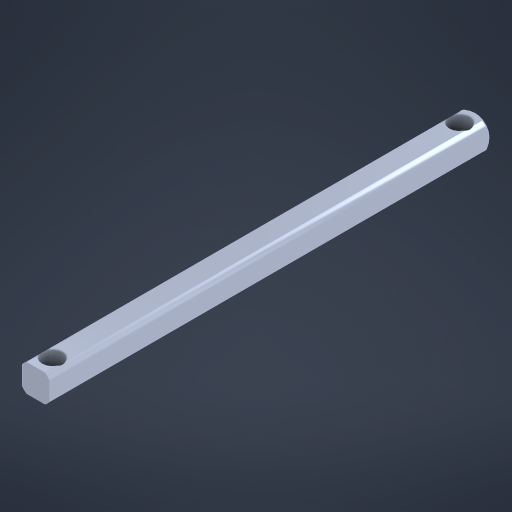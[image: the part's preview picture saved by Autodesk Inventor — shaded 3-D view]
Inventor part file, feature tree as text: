
AUTODESK INVENTOR PART (.ipt)
format: ipt  version: 2024 (Build 280153000, 153)  size: 310,784 bytes
history: native  units: in
note: dims shown in document units (in); Inventor stores cm internally (conversion verified against a paired STEP export)
features: other x50, sketch x3, extrude x2, thicken_offset x1, hole x1
ambient origin geometry x8: Origin, YZ Plane, XZ Plane, XY Plane, X Axis, Y Axis, Z Axis, Center Point
bodies: Solid1 (feature_tree)
feature tree (57):
  other  "Table"
  other  "Shaft HS 0.5 in"
  other  "Shaft HS 1.0 in"
  other  "Shaft HS 1.5 in"
  other  "Shaft HS 2.0 in"
  other  "Shaft HS 2.5 in"
  other  "Shaft HS 3.0 in"
  other  "Shaft HS 3.5 in"
  other  "Shaft HS 4.0 in"
  other  "Shaft HS 4.5 in"
  other  "Shaft HS 5.0 in"
  other  "Shaft HS 5.5 in"
  other  "Shaft HS 6.0 in"
  other  "Shaft HS 6.5 in"
  other  "Shaft HS 7.0 in"
  other  "Shaft HS 7.5 in"
  other  "Shaft HS 8.0 in"
  other  "Shaft HS 8.5 in"
  other  "Shaft HS 9.0 in"
  other  "Shaft HS 9.5 in"
  other  "Shaft HS 10.0 in"
  other  "Shaft HS 10.5 in"
  other  "Shaft HS 11.0 in"
  other  "Shaft HS 11.5 in"
  other  "Shaft HS 12.0 in"
  other  "Shaft HS 12.5 in"
  other  "Shaft HS 13.0 in"
  other  "Shaft HS 13.5 in"
  other  "Shaft HS 14.0 in"
  other  "Shaft HS 14.5 in"
  other  "Shaft HS 15.0 in"
  other  "Shaft HS 15.5 in"
  other  "Shaft HS 16.0 in"
  other  "Shaft HS 16.5 in"
  other  "Shaft HS 17.0 in"
  other  "Shaft HS 17.5 in"
  other  "Shaft HS 18.0 in"
  other  "Shaft HS 18.5 in"
  other  "Shaft HS 19.0 in"
  other  "Shaft HS 19.5 in"
  other  "Shaft HS 20.0 in"
  other  "Shaft HS 20.5 in"
  other  "Shaft HS 21.0 in"
  other  "Shaft HS 21.5 in"
  other  "Shaft HS 22.0 in"
  other  "Shaft HS 22.5 in"
  other  "Shaft HS 23.0 in"
  other  "Shaft HS 23.5 in"
  other  "Shaft HS 24.0 in"
  extrude  "Extrusion1"  Depth=12.1875in
  thicken_offset  "Thicken1"
  extrude  "Extrusion2"  Depth=20.125in
  hole  "Hole1"  [1 undecoded]
  sketch  "Sketch2"  dims[d0=0.0625in d1=0.0in d2=12.1875in]
  sketch  "Sketch3"  dims[d3=12.125in d4=20.125in]
  sketch  "Sketch6"  dims[d5=0.0in d9=0.15in d11=0.1875in d12=0.75in d13=0.375in d14=0.25in d15=0.5635in d16=1.0in d17=0.8108in d18=3.7in]
  other  "Cut-Revolve3"
note: 1 required parameter value undecoded (feature->parameter linkage not recoverable at this tier; creation-order binding heuristic only, values carry confidence <= 0.55)
